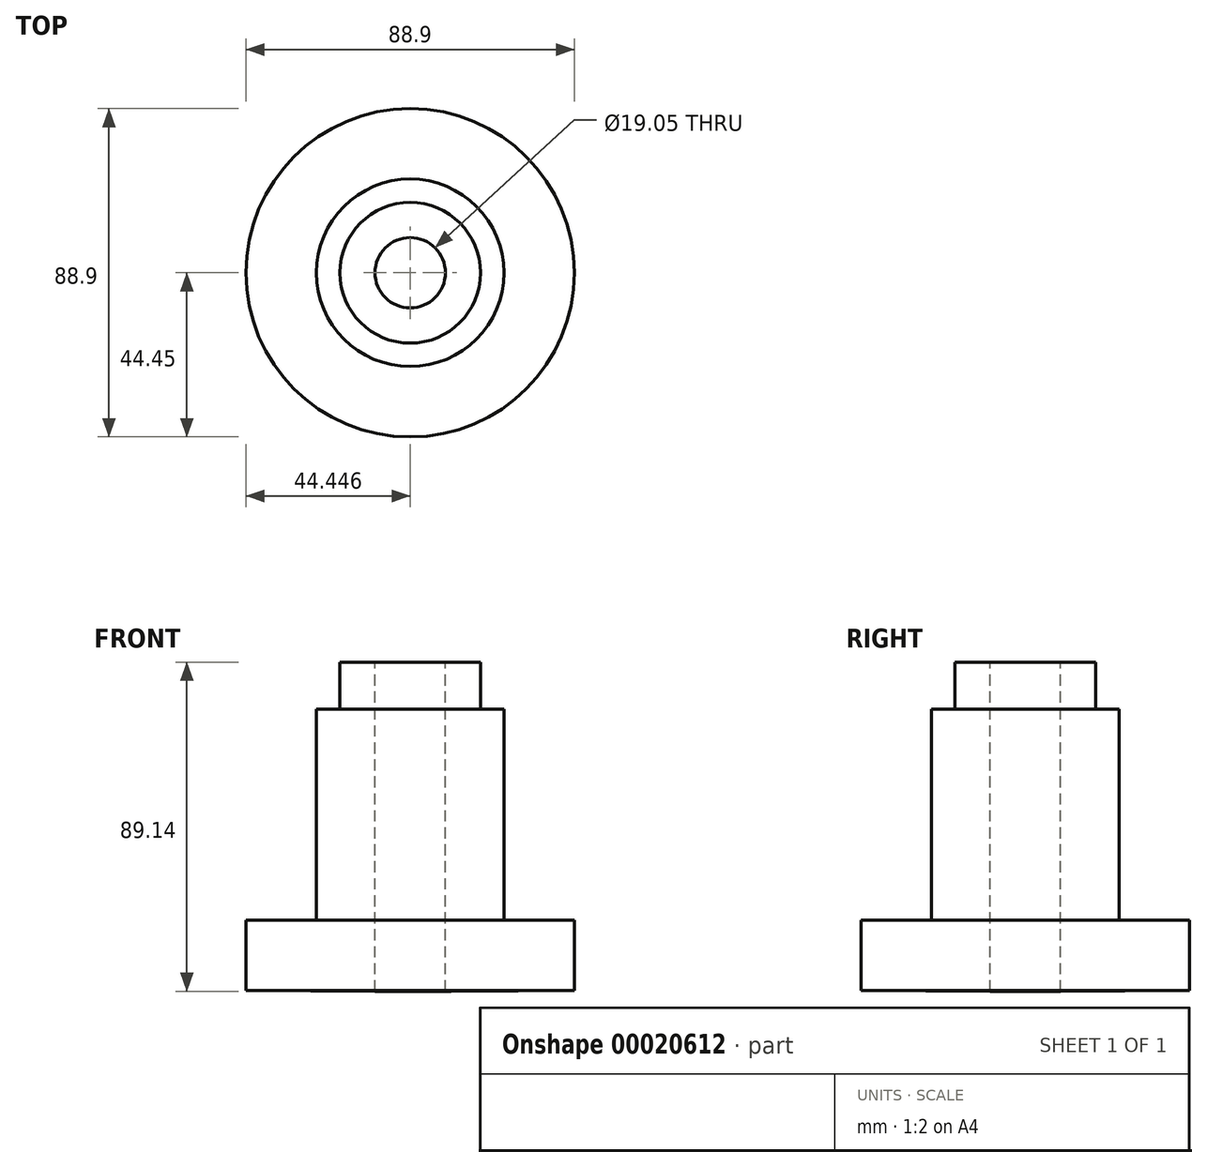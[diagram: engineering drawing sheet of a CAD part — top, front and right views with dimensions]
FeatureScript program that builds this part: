
annotation { "Feature Type Name" : "Feature", "Feature Type Description" : "" }
export const myFeature = defineFeature(function(context is Context, id is Id, definition is map)
    precondition{}
    {
        {
            var Q0;
            Q0=qCreatedBy(makeId("Front.planeOp"),FACE);
            var sketch = newSketch(context, id + "F0", { "sketchPlane" : qUnion([Q0])});
            skLineSegment(sketch, "E0", {"start": v(52.72, -41.34) * mm, "end": v(52.72, -22.3) * mm});
            skLineSegment(sketch, "E1", {"start": v(52.72, -22.3) * mm, "end": v(33.67, -22.3) * mm});
            skLineSegment(sketch, "E2", {"start": v(33.67, -22.3) * mm, "end": v(33.67, 34.86) * mm});
            skLineSegment(sketch, "E3", {"start": v(33.67, 34.86) * mm, "end": v(27.32, 34.86) * mm});
            skLineSegment(sketch, "E4", {"start": v(27.32, 34.86) * mm, "end": v(27.32, 47.56) * mm});
            skLineSegment(sketch, "E5", {"start": v(27.32, 47.56) * mm, "end": v(17.8, 47.56) * mm});
            skLineSegment(sketch, "E6", {"start": v(8.27, 47.56) * mm, "end": v(8.27, -41.77) * mm});
            skPoint(sketch, "E7.end.orphan", {"position": v(52.72, -41.77) * mm});
            skLineSegment(sketch, "E8", {"start": v(17.8, 47.56) * mm, "end": v(17.8, -41.58) * mm});
            skLineSegment(sketch, "E9", {"start": v(17.8, -41.58) * mm, "end": v(52.72, -41.34) * mm});
            skSolve(sketch);
        }
        {
            var Q0;
            Q0=makeQuery(id+"F0.imprint","IMPRINT",FACE,{"disambiguationData":[TD([[makeQuery(id+"F0.imprint","IMPRINT",EDGE,{"derivedFrom":sQuery(id+"F0.wireOp",EDGE,"E0")}),1.0]])]});
            var Q1;
            Q1=sQuery(id+"F0.wireOp",EDGE,"E6");
            revolve(context, id + "F1", {"entities" : qUnion([Q0]), "axis" : qUnion([Q1]), "revolveType" : RevolveType.FULL});
        }
    });
